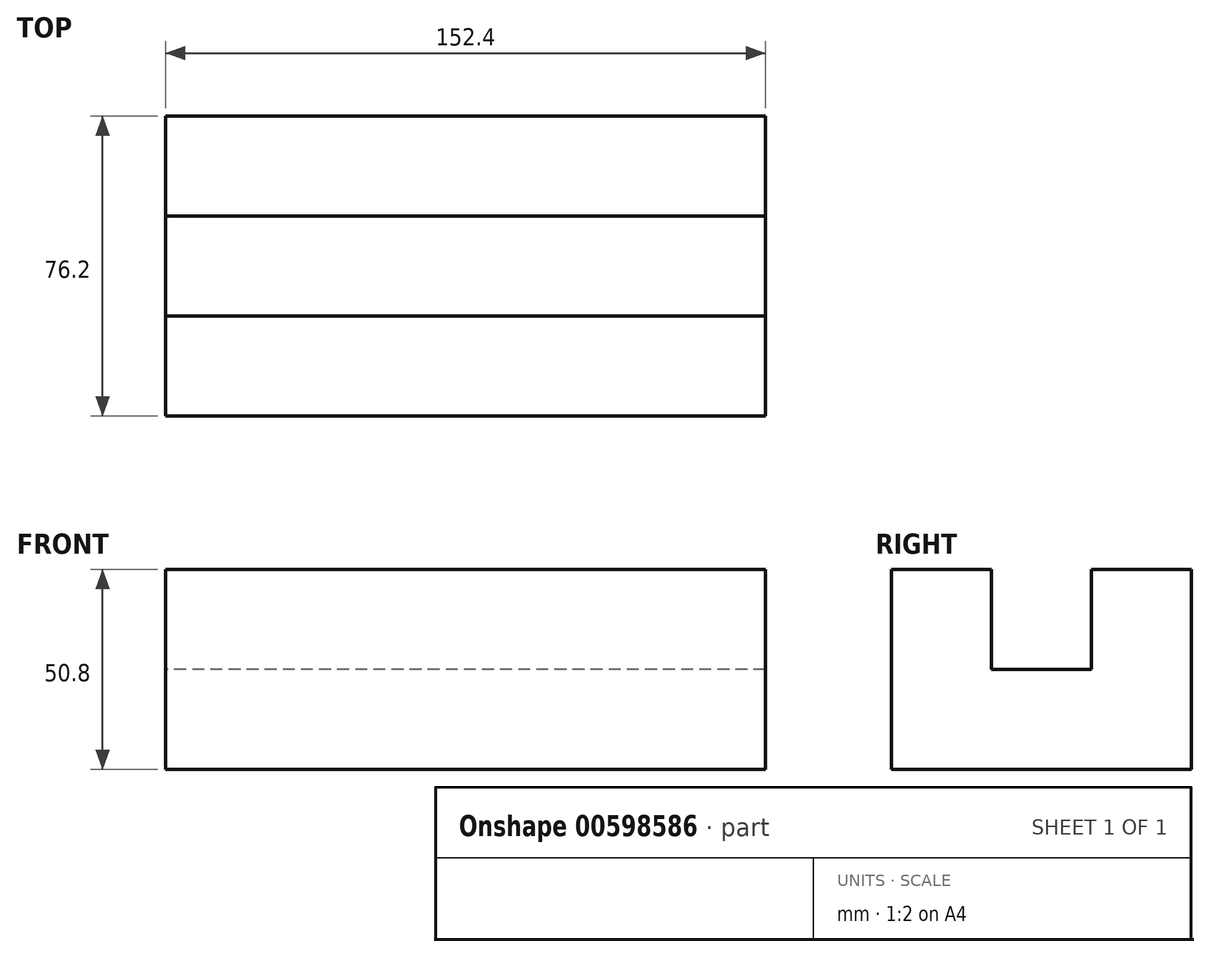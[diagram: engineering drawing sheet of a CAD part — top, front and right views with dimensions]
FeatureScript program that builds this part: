
annotation { "Feature Type Name" : "Feature", "Feature Type Description" : "" }
export const myFeature = defineFeature(function(context is Context, id is Id, definition is map)
    precondition{}
    {
        {
            var Q0;
            Q0=qCreatedBy(makeId("Right.planeOp"),FACE);
            var sketch = newSketch(context, id + "F0", { "sketchPlane" : qUnion([Q0])});
            skLineSegment(sketch, "E0", {"start": v(0, 0) * mm, "end": v(76.2, 0) * mm});
            skLineSegment(sketch, "E1", {"start": v(76.2, 0) * mm, "end": v(76.2, 50.8) * mm});
            skLineSegment(sketch, "E2", {"start": v(76.2, 50.8) * mm, "end": v(50.8, 50.8) * mm});
            skLineSegment(sketch, "E3", {"start": v(50.8, 50.8) * mm, "end": v(50.8, 25.4) * mm});
            skLineSegment(sketch, "E4", {"start": v(50.8, 25.4) * mm, "end": v(25.4, 25.4) * mm});
            skLineSegment(sketch, "E5", {"start": v(25.4, 25.4) * mm, "end": v(25.4, 50.8) * mm});
            skLineSegment(sketch, "E6", {"start": v(25.4, 50.8) * mm, "end": v(0, 50.8) * mm});
            skLineSegment(sketch, "E7", {"start": v(0, 50.8) * mm, "end": v(0, 0) * mm});
            skSolve(sketch);
        }
        {
            var Q0;
            Q0 = qSketchRegion(id + "F0", true);
            extrude(context, id + "F1", {"entities" : qUnion([Q0]), "depth" : 152.4 * mm, "offsetDistance" : 25.4 * mm});
        }
    });
